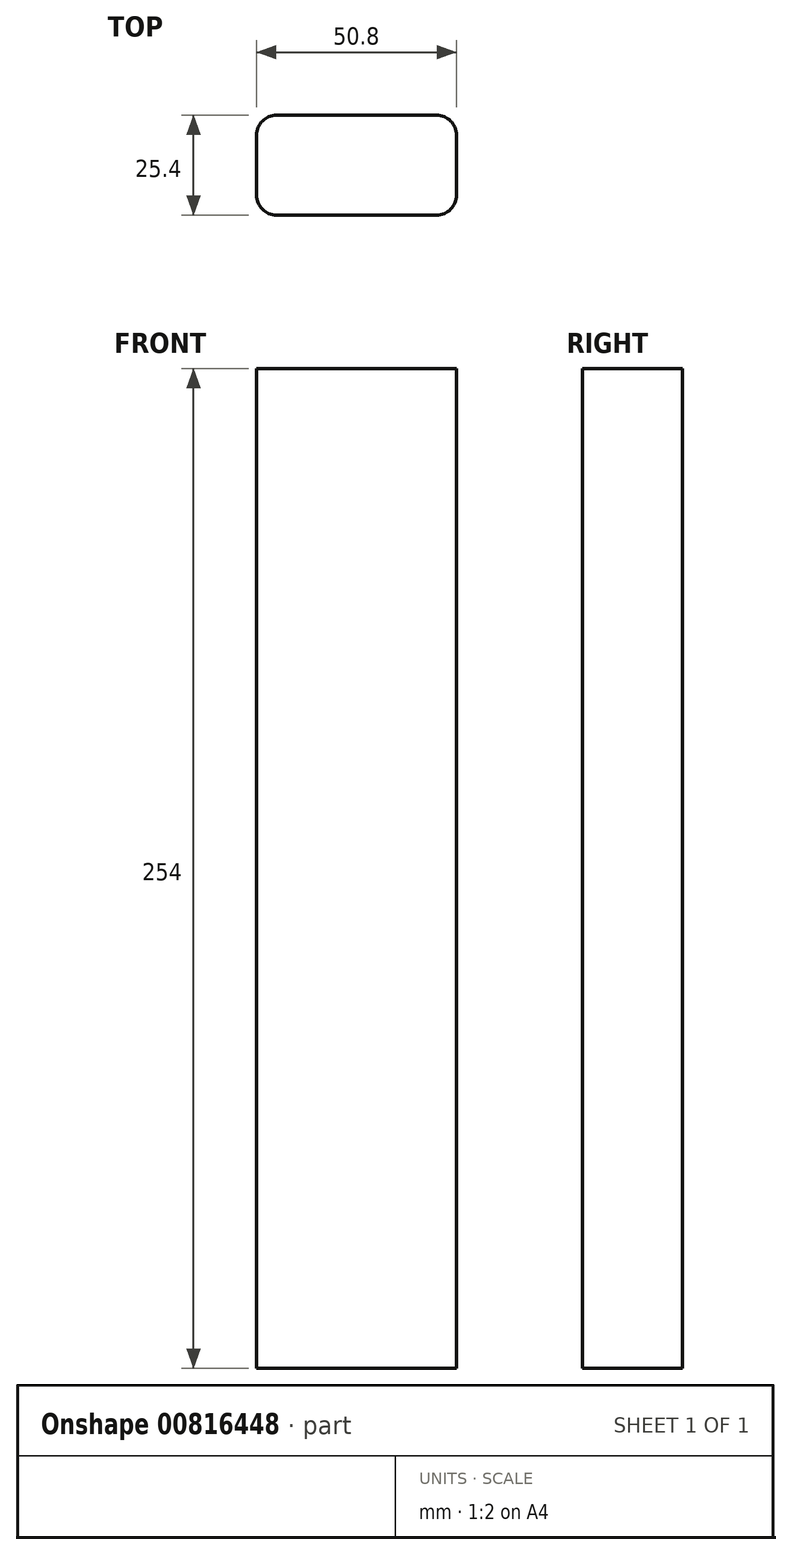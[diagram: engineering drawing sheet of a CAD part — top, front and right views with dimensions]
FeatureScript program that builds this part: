
annotation { "Feature Type Name" : "Feature", "Feature Type Description" : "" }
export const myFeature = defineFeature(function(context is Context, id is Id, definition is map)
    precondition{}
    {
        {
            var Q0;
            Q0=qCreatedBy(makeId("Top.planeOp"),FACE);
            var sketch = newSketch(context, id + "F0", { "sketchPlane" : qUnion([Q0])});
            skLineSegment(sketch, "E0.bottom", {"start": v(-18.42, 10.13) * mm, "end": v(22.22, 10.13) * mm});
            skLineSegment(sketch, "E0.top", {"start": v(-18.42, -15.27) * mm, "end": v(22.22, -15.27) * mm});
            skLineSegment(sketch, "E0.left", {"start": v(-23.5, 5.05) * mm, "end": v(-23.5, -10.19) * mm});
            skLineSegment(sketch, "E0.right", {"start": v(27.3, 5.05) * mm, "end": v(27.3, -10.19) * mm});
            skPoint(sketch, "E1.visualSharp", {"position": v(-23.5, 10.13) * mm});
            skArc(sketch, "E1.filletArc", {"start": v(-18.42, 10.13) * mm, "mid": v(-22, 8.65) * mm, "end": v(-23.5, 5.05) * mm});
            skPoint(sketch, "E2.visualSharp", {"position": v(27.3, 10.13) * mm});
            skArc(sketch, "E2.filletArc", {"start": v(27.3, 5.05) * mm, "mid": v(25.82, 8.65) * mm, "end": v(22.22, 10.13) * mm});
            skPoint(sketch, "E3.visualSharp", {"position": v(27.3, -15.27) * mm});
            skArc(sketch, "E3.filletArc", {"start": v(22.22, -15.27) * mm, "mid": v(25.82, -13.78) * mm, "end": v(27.3, -10.19) * mm});
            skPoint(sketch, "E4.visualSharp", {"position": v(-23.5, -15.27) * mm});
            skArc(sketch, "E4.filletArc", {"start": v(-23.5, -10.19) * mm, "mid": v(-22, -13.78) * mm, "end": v(-18.42, -15.27) * mm});
            skSolve(sketch);
        }
        {
            var Q0;
            Q0=makeQuery(id+"F0.imprint","IMPRINT",FACE,{"disambiguationData":[TD([[makeQuery(id+"F0.imprint","IMPRINT",EDGE,{"derivedFrom":sQuery(id+"F0.wireOp",EDGE,"E0.bottom")}),-1.0]])]});
            extrude(context, id + "F1", {"entities" : qUnion([Q0]), "depth" : 254 * mm, "offsetDistance" : 25.4 * mm});
        }
    });
